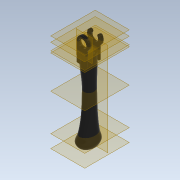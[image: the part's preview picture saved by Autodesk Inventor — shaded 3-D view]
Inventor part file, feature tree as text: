
AUTODESK INVENTOR PART (.ipt)
format: ipt  version: 2020.2 (Build 242310000, 310)  size: 423,936 bytes
history: native  units: mm
features: sketch x15, plane x9, extrude x6, loft x1, fillet x1, sweep x1
ambient origin geometry x8: Origin, YZ Plane, XZ Plane, XY Plane, X Axis, Y Axis, Z Axis, Center Point
bodies: Solid1 (feature_tree)
feature tree (33):
  plane  "Work Plane1"
  plane  "Work Plane2"
  plane  "Work Plane5"
  plane  "Work Plane6"
  loft  "Loft1"
  plane  "Work Plane7"
  extrude  "Extrusion1"  Depth=25.0mm
  plane  "Work Plane8"
  extrude  "Extrusion2"  TaperAngle=0.0deg  [1 undecoded]
  extrude  "Extrusion3"  TaperAngle=0.0deg  [1 undecoded]
  extrude  "Extrusion4"  TaperAngle=0.0deg  [1 undecoded]
  plane  "Work Plane9"
  extrude  "Extrusion5"  [1 undecoded]
  fillet  "Fillet1"  Radius=35.004mm
  sketch  "Sketch13"  dims[d47=20.0mm]
  extrude  "Extrusion6"  Depth=7.0mm TaperAngle=0.0deg
  sweep  "Sweep1"
  sketch  "Sketch1"  dims[d0=20.0mm d1=100.0mm]
  sketch  "Sketch2"  dims[d2=90.0mm d3=25.0mm d4=15.0mm d5=-15.0mm]
  sketch  "Sketch3"  dims[d6=200.0mm d7=90.0deg d8=0.0mm d9=90.0deg]
  plane  "Work Plane3"
  plane  "Work Plane4"
  sketch  "Sketch4"  dims[d10=0.0mm d11=90.0deg d12=0.0mm d13=90.0deg]
  sketch  "Sketch5"  dims[d14=0.0mm d15=90.0deg d16=0.0mm d17=90.0deg]
  sketch  "Sketch6"  dims[d18=200.0mm d19=90.0deg d20=-35.0mm d21=35.004mm d22=0.0mm]
  sketch  "Sketch7"  dims[d23=-22.0mm d39=7.0mm d40=0.0mm]
  sketch  "Sketch8"  dims[d41=25.0mm d42=55.0mm d43=0.0mm]
  sketch  "Sketch10"  dims[d44=15.0mm]
  sketch  "Sketch11"  dims[d45=20.0mm]
  sketch  "Sketch12"  dims[d46=31.0mm]
  sketch  "Sketch14"  dims[d48=11.5mm d49=0.0mm]
  sketch  "Sketch15"  dims[d50=2.75mm]
  sketch  "Sketch16"  dims[d54=28.0mm d61=5.0mm d62=0.0mm d66=15.0mm d67=90.0deg d68=15.0mm d69=15.0mm d70=120.0deg d71=120.0deg d72=2.0mm d73=2.0mm d74=2.0mm d75=135.0deg d76=45.0deg d77=40.0mm d78=15.0mm d79=12.0mm d80=22.0mm d81=35.0mm d82=3.0mm d83=3.0mm d84=0.0mm d85=8.0mm d86=0.0mm d87=0.0mm]
note: 4 required parameter values undecoded (feature->parameter linkage not recoverable at this tier; creation-order binding heuristic only, values carry confidence <= 0.55)
